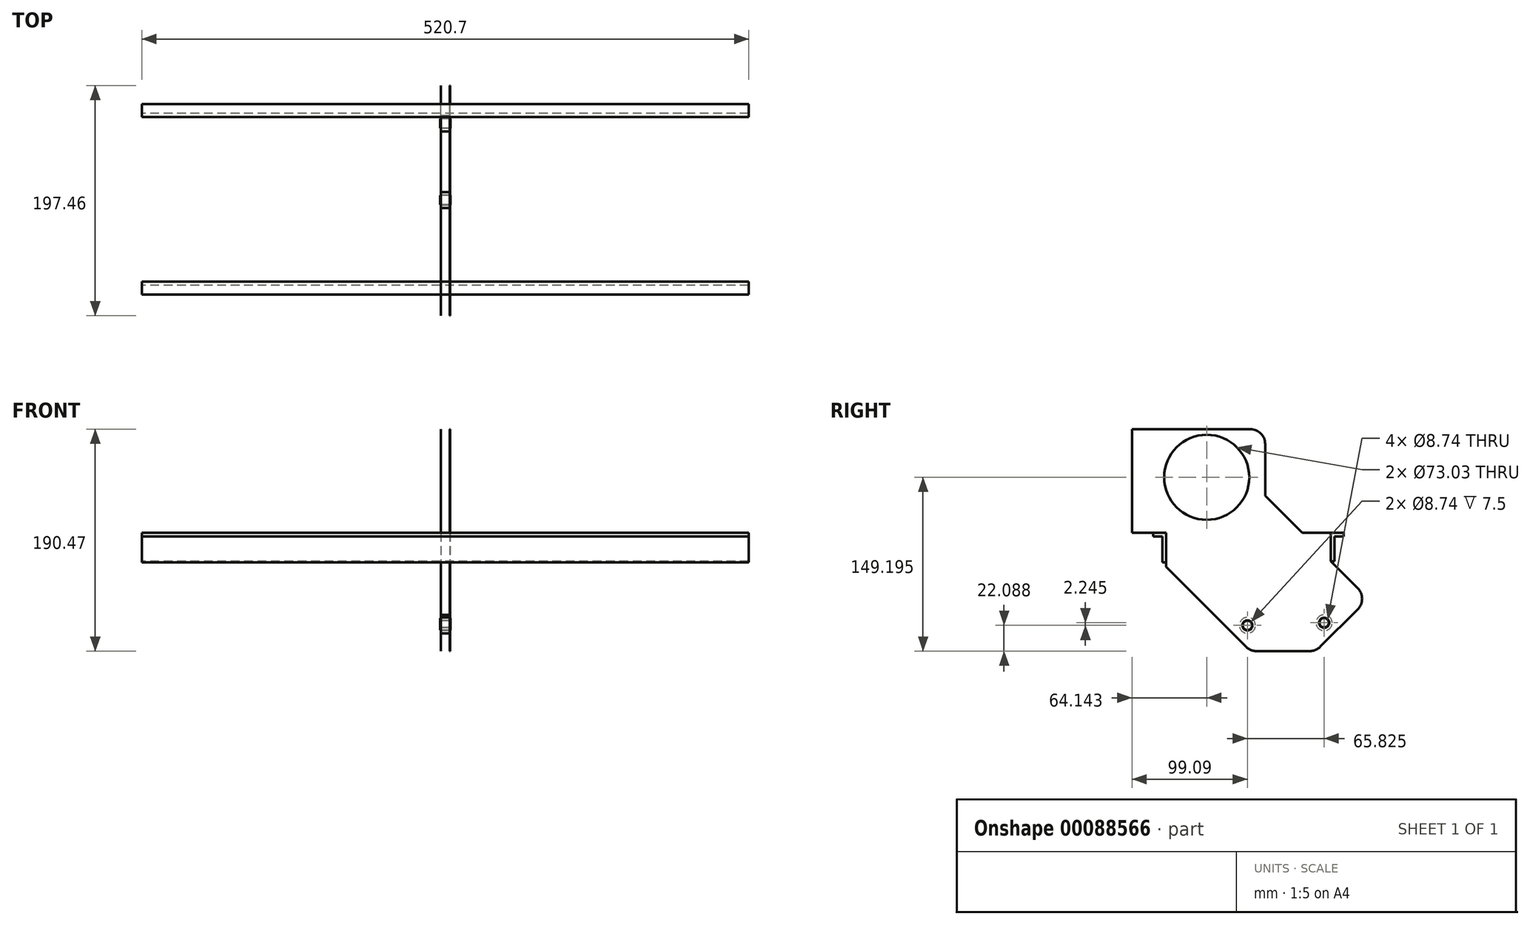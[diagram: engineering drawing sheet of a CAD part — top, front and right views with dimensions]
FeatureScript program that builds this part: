
annotation { "Feature Type Name" : "Feature", "Feature Type Description" : "" }
export const myFeature = defineFeature(function(context is Context, id is Id, definition is map)
    precondition{}
    {
        {
            assignVariable(context, id + "F0", {"name" : "wBatt", "anyValue" : 7});
        }
        {
            assignVariable(context, id + "F1", {"name" : "tPlate", "anyValue" : 1 / 4});
        }
        {
            var Q0;
            Q0=qCreatedBy(makeId("Right.planeOp"),FACE);
            var sketch = newSketch(context, id + "F2", { "sketchPlane" : qUnion([Q0])});
            skLineSegment(sketch, "E0.bottom", {"start": v(0, 0) * mm, "end": v(-19.05, 0) * mm});
            skLineSegment(sketch, "E0.top", {"start": v(0, -88.9) * mm, "end": v(-19.05, -88.9) * mm});
            skLineSegment(sketch, "E0.left", {"start": v(0, 0) * mm, "end": v(0, -88.9) * mm});
            skLineSegment(sketch, "E0.right", {"start": v(-19.05, 0) * mm, "end": v(-19.05, -88.9) * mm});
            skLineSegment(sketch, "E1", {"start": v(-45.67, -13.92) * mm, "end": v(130.88, -190.47) * mm, "construction": true});
            skLineSegment(sketch, "E2", {"start": v(130.88, -190.47) * mm, "end": v(189.25, -132.1) * mm, "construction": true});
            skLineSegment(sketch, "E3", {"start": v(189.25, -132.1) * mm, "end": v(71.07, -13.92) * mm, "construction": true});
            skCircle(sketch, "E4", {"center": v(64.14, -41.27) * mm, "radius": 36.51 * mm, "construction": true});
            skCircle(sketch, "E5", {"center": v(99.1, -168.38) * mm, "radius": 6.86 * mm});
            skCircle(sketch, "E6", {"center": v(164.92, -166.14) * mm, "radius": 6.86 * mm});
            skPoint(sketch, "E7", {"position": v(160.07, -161.29) * mm});
            skPoint(sketch, "E8", {"position": v(103.94, -163.53) * mm});
            skCircle(sketch, "E9", {"center": v(99.1, -168.38) * mm, "radius": 4.37 * mm});
            skCircle(sketch, "E10", {"center": v(164.92, -166.14) * mm, "radius": 4.37 * mm});
            skLineSegment(sketch, "E11", {"start": v(0, -88.9) * mm, "end": v(146.05, -88.9) * mm, "construction": true});
            skLineSegment(sketch, "E12.bottom", {"start": v(146.05, -84.14) * mm, "end": v(400.05, -84.14) * mm, "construction": true});
            skLineSegment(sketch, "E12.top", {"start": v(146.05, -88.9) * mm, "end": v(400.05, -88.9) * mm, "construction": true});
            skLineSegment(sketch, "E12.left", {"start": v(146.05, -84.14) * mm, "end": v(146.05, -88.9) * mm, "construction": true});
            skLineSegment(sketch, "E12.right", {"start": v(400.05, -84.14) * mm, "end": v(400.05, -88.9) * mm, "construction": true});
            skLineSegment(sketch, "E13", {"start": v(170.5, -88.9) * mm, "end": v(170.5, -113.34) * mm});
            skLineSegment(sketch, "E14", {"start": v(170.5, -113.34) * mm, "end": v(173.67, -113.34) * mm});
            skLineSegment(sketch, "E15", {"start": v(173.67, -113.34) * mm, "end": v(173.67, -92.08) * mm});
            skLineSegment(sketch, "E16", {"start": v(173.67, -92.07) * mm, "end": v(181.6, -92.07) * mm});
            skLineSegment(sketch, "E17", {"start": v(181.6, -92.08) * mm, "end": v(181.6, -88.9) * mm});
            skLineSegment(sketch, "E18", {"start": v(181.6, -88.9) * mm, "end": v(170.5, -88.9) * mm});
            skLineSegment(sketch, "E19", {"start": v(71.07, -13.92) * mm, "end": v(12.7, -72.3) * mm, "construction": true});
            skPoint(sketch, "E20", {"position": v(184.15, -88.9) * mm});
            skCircle(sketch, "E21", {"center": v(184.15, -88.9) * mm, "radius": 177.8 * mm, "construction": true});
            skLineSegment(sketch, "E22", {"start": v(18.2, -88.9) * mm, "end": v(29.3, -88.9) * mm});
            skLineSegment(sketch, "E23", {"start": v(29.3, -88.9) * mm, "end": v(29.3, -114.3) * mm});
            skLineSegment(sketch, "E24", {"start": v(29.3, -114.3) * mm, "end": v(26.13, -114.3) * mm});
            skLineSegment(sketch, "E25", {"start": v(26.13, -114.3) * mm, "end": v(26.13, -92.07) * mm});
            skLineSegment(sketch, "E26", {"start": v(26.13, -92.07) * mm, "end": v(18.2, -92.07) * mm});
            skLineSegment(sketch, "E27", {"start": v(18.2, -92.07) * mm, "end": v(18.2, -88.9) * mm});
            skCircle(sketch, "E28", {"center": v(99.1, -168.38) * mm, "radius": 3.97 * mm});
            skCircle(sketch, "E29", {"center": v(164.92, -166.14) * mm, "radius": 3.97 * mm});
            skSolve(sketch);
        }
        {
            var Q0;
            Q0=qCreatedBy(makeId("Right.planeOp"),FACE);
            var sketch = newSketch(context, id + "F3", { "sketchPlane" : qUnion([Q0])});
            skCircle(sketch, "E30.0", {"center": v(64.14, -41.27) * mm, "radius": 36.51 * mm, "construction": true});
            skSolve(sketch);
        }
        {
            var Q0;
            Q0=makeQuery(id+"F2.imprint","IMPRINT",FACE,{"disambiguationData":[TD([[makeQuery(id+"F2.imprint","IMPRINT",EDGE,{"derivedFrom":sQuery(id+"F2.wireOp",EDGE,"E22")}),-1.0]])]});
            var Q1;
            Q1=makeQuery(id+"F2.imprint","IMPRINT",FACE,{"disambiguationData":[TD([[makeQuery(id+"F2.imprint","IMPRINT",EDGE,{"derivedFrom":sQuery(id+"F2.wireOp",EDGE,"E13")}),1.0]])]});
            extrude(context, id + "F4", {"entities" : qUnion([Q0, Q1]), "depth" : 260.35 * mm, "hasSecondDirection" : true, "secondDirectionOppositeDirection" : true, "secondDirectionDepth" : 260.35 * mm});
        }
        {
            var Q0;
            Q0=makeQuery(id+"F2.imprint","IMPRINT",FACE,{"disambiguationData":[TD([[makeQuery(id+"F2.imprint","IMPRINT",EDGE,{"derivedFrom":sQuery(id+"F2.wireOp",EDGE,"E6")}),1.0]])]});
            var Q1;
            Q1=makeQuery(id+"F2.imprint","IMPRINT",FACE,{"disambiguationData":[TD([[makeQuery(id+"F2.imprint","IMPRINT",EDGE,{"derivedFrom":sQuery(id+"F2.wireOp",EDGE,"E5")}),1.0]])]});
            extrude(context, id + "F5", {"entities" : qUnion([Q0, Q1]), "depth" : (getVariable(context, 'wBatt') / 2 + .25) * mm, "hasSecondDirection" : true, "secondDirectionOppositeDirection" : true, "secondDirectionDepth" : (getVariable(context, 'wBatt') / 2 + .25) * mm});
        }
        {
            var Q0;
            Q0=makeQuery(id+"F2.imprint","IMPRINT",FACE,{"disambiguationData":[TD([[makeQuery(id+"F2.imprint","IMPRINT",EDGE,{"derivedFrom":sQuery(id+"F2.wireOp",EDGE,"E28")}),1.0]])]});
            var Q1;
            Q1=makeQuery(id+"F2.imprint","IMPRINT",FACE,{"disambiguationData":[TD([[makeQuery(id+"F2.imprint","IMPRINT",EDGE,{"derivedFrom":sQuery(id+"F2.wireOp",EDGE,"E29")}),1.0]])]});
            extrude(context, id + "F6", {"entities" : qUnion([Q0, Q1]), "depth" : (getVariable(context, 'wBatt') / 2 + .25 + getVariable(context, 'tPlate') + .5) * mm, "hasSecondDirection" : true, "secondDirectionOppositeDirection" : true, "secondDirectionDepth" : (getVariable(context, 'wBatt') / 2 + .25 + getVariable(context, 'tPlate') + .5) * mm});
        }
        {
            var Q0;
            Q0=makeQuery(id+"F5.opExtrude","CAP_FACE",FACE,{"disambiguationData":[OSD([sQuery(id+"F2.wireOp",EDGE,"E6"),sQuery(id+"F2.wireOp",EDGE,"E10")])],"isStart":false});
            var sketch = newSketch(context, id + "F7", { "sketchPlane" : qUnion([Q0])});
            skLineSegment(sketch, "E31.0", {"start": v(29.3, -88.9) * mm, "end": v(29.3, -114.3) * mm, "construction": true});
            skLineSegment(sketch, "E32", {"start": v(106.83, -190.47) * mm, "end": v(152.56, -190.47) * mm});
            skLineSegment(sketch, "E33", {"start": v(161.54, -186.75) * mm, "end": v(193.74, -154.55) * mm});
            skLineSegment(sketch, "E34", {"start": v(146.05, -88.9) * mm, "end": v(114.3, -57.15) * mm});
            skLineSegment(sketch, "E35", {"start": v(114.3, -57.15) * mm, "end": v(114.3, -12.7) * mm});
            skLineSegment(sketch, "E36", {"start": v(101.6, 0) * mm, "end": v(0, 0) * mm});
            skLineSegment(sketch, "E37", {"start": v(0, 0) * mm, "end": v(0, -88.9) * mm});
            skLineSegment(sketch, "E38", {"start": v(0, -88.9) * mm, "end": v(29.3, -88.9) * mm});
            skLineSegment(sketch, "E39", {"start": v(29.3, -88.9) * mm, "end": v(29.3, -118.2) * mm});
            skLineSegment(sketch, "E40", {"start": v(29.3, -118.2) * mm, "end": v(97.85, -186.75) * mm});
            skLineSegment(sketch, "E41.0", {"start": v(170.5, -88.9) * mm, "end": v(170.5, -113.34) * mm});
            skLineSegment(sketch, "E42", {"start": v(146.05, -88.9) * mm, "end": v(170.5, -88.9) * mm});
            skLineSegment(sketch, "E43", {"start": v(170.5, -113.34) * mm, "end": v(193.74, -136.6) * mm});
            skPoint(sketch, "E44.visualSharp", {"position": v(114.3, 0) * mm});
            skArc(sketch, "E44.filletArc", {"start": v(114.3, -12.7) * mm, "mid": v(110.58, -3.72) * mm, "end": v(101.6, 0) * mm});
            skPoint(sketch, "E45.visualSharp", {"position": v(202.72, -145.57) * mm});
            skArc(sketch, "E45.filletArc", {"start": v(193.74, -154.55) * mm, "mid": v(197.46, -145.57) * mm, "end": v(193.74, -136.6) * mm});
            skPoint(sketch, "E46.visualSharp", {"position": v(157.82, -190.47) * mm});
            skArc(sketch, "E46.filletArc", {"start": v(152.56, -190.47) * mm, "mid": v(157.42, -189.5) * mm, "end": v(161.54, -186.75) * mm});
            skPoint(sketch, "E47.visualSharp", {"position": v(101.57, -190.47) * mm});
            skArc(sketch, "E47.filletArc", {"start": v(97.85, -186.75) * mm, "mid": v(101.97, -189.5) * mm, "end": v(106.83, -190.47) * mm});
            skCircle(sketch, "E48.0", {"center": v(64.14, -41.27) * mm, "radius": 36.51 * mm});
            skCircle(sketch, "E49.0", {"center": v(99.1, -168.38) * mm, "radius": 4.37 * mm});
            skCircle(sketch, "E50.0", {"center": v(164.92, -166.14) * mm, "radius": 4.37 * mm});
            skLineSegment(sketch, "E51", {"start": v(-44.45, -44.45) * mm, "end": v(53.43, 53.43) * mm, "construction": true});
            skLineSegment(sketch, "E52", {"start": v(-44.45, -44.45) * mm, "end": v(129.7, -218.6) * mm, "construction": true});
            skLineSegment(sketch, "E53", {"start": v(53.43, 53.43) * mm, "end": v(227.58, -120.72) * mm, "construction": true});
            skLineSegment(sketch, "E54", {"start": v(227.58, -120.72) * mm, "end": v(129.7, -218.6) * mm, "construction": true});
            skSolve(sketch);
        }
        {
            var Q0;
            Q0=makeQuery(id+"F7.imprint","IMPRINT",FACE,{"disambiguationData":[TD([[makeQuery(id+"F7.imprint","IMPRINT",EDGE,{"derivedFrom":sQuery(id+"F7.wireOp",EDGE,"E32")}),1.0]])]});
            var Q1;
            Q1=makeQuery(id+"F7.imprint","IMPRINT",FACE,{"disambiguationData":[TD([[makeQuery(id+"F7.imprint","IMPRINT",EDGE,{"derivedFrom":sQuery(id+"F7.wireOp",EDGE,"E50.0")}),-1.0]])]});
            extrude(context, id + "F8", {"entities" : qUnion([Q0, Q1]), "depth" : (getVariable(context, 'tPlate')) * mm});
        }
        {
            var Q0;
            Q0=makeQuery(id+"F8.opExtrude","SWEPT_BODY",BODY,{"disambiguationData":[OSD([sQuery(id+"F7.wireOp",EDGE,"E32"),sQuery(id+"F7.wireOp",EDGE,"E33"),sQuery(id+"F7.wireOp",EDGE,"E34"),sQuery(id+"F7.wireOp",EDGE,"E35"),sQuery(id+"F7.wireOp",EDGE,"E36"),sQuery(id+"F7.wireOp",EDGE,"E37"),sQuery(id+"F7.wireOp",EDGE,"E38"),sQuery(id+"F7.wireOp",EDGE,"E39"),sQuery(id+"F7.wireOp",EDGE,"E40"),sQuery(id+"F7.wireOp",EDGE,"E41.0"),sQuery(id+"F7.wireOp",EDGE,"E42"),sQuery(id+"F7.wireOp",EDGE,"E43"),sQuery(id+"F7.wireOp",EDGE,"E44.filletArc"),sQuery(id+"F7.wireOp",EDGE,"E45.filletArc"),sQuery(id+"F7.wireOp",EDGE,"E46.filletArc"),sQuery(id+"F7.wireOp",EDGE,"E47.filletArc"),sQuery(id+"F7.wireOp",EDGE,"E48.0"),sQuery(id+"F7.wireOp",EDGE,"E49.0"),sQuery(id+"F7.wireOp",EDGE,"E50.0")])]});
            var Q1;
            Q1=qCreatedBy(makeId("Right.planeOp"),FACE);
            mirror(context, id + "F9", {"entities" : qUnion([Q0]), "mirrorPlane" : qUnion([Q1])});
        }
    });
